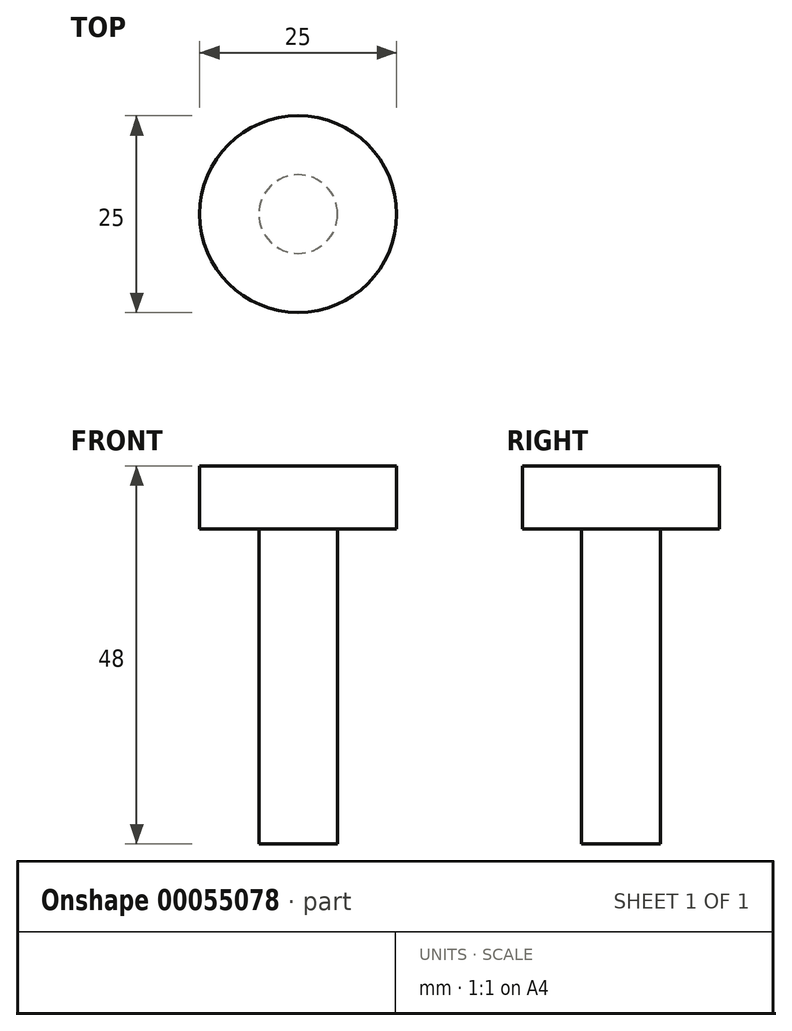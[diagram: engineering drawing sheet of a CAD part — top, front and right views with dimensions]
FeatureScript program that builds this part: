
annotation { "Feature Type Name" : "Feature", "Feature Type Description" : "" }
export const myFeature = defineFeature(function(context is Context, id is Id, definition is map)
    precondition{}
    {
        {
            var Q0;
            Q0=qCreatedBy(makeId("Top.planeOp"),FACE);
            var sketch = newSketch(context, id + "F0", { "sketchPlane" : qUnion([Q0])});
            skCircle(sketch, "E0", {"center": v(0, 0) * mm, "radius": 5 * mm});
            skSolve(sketch);
        }
        {
            var Q0;
            Q0 = qSketchRegion(id + "F0", true);
            extrude(context, id + "F1", {"entities" : qUnion([Q0]), "oppositeDirection" : true, "depth" : 40 * mm});
        }
        {
            var Q0;
            Q0=qCreatedBy(makeId("Top.planeOp"),FACE);
            var sketch = newSketch(context, id + "F2", { "sketchPlane" : qUnion([Q0])});
            skCircle(sketch, "E1", {"center": v(0, 0) * mm, "radius": 12.5 * mm});
            skSolve(sketch);
        }
        {
            var Q0;
            Q0 = qSketchRegion(id + "F2", true);
            extrude(context, id + "F3", {"entities" : qUnion([Q0]), "operationType" : NewBodyOperationType.ADD, "depth" : 8 * mm});
        }
    });
